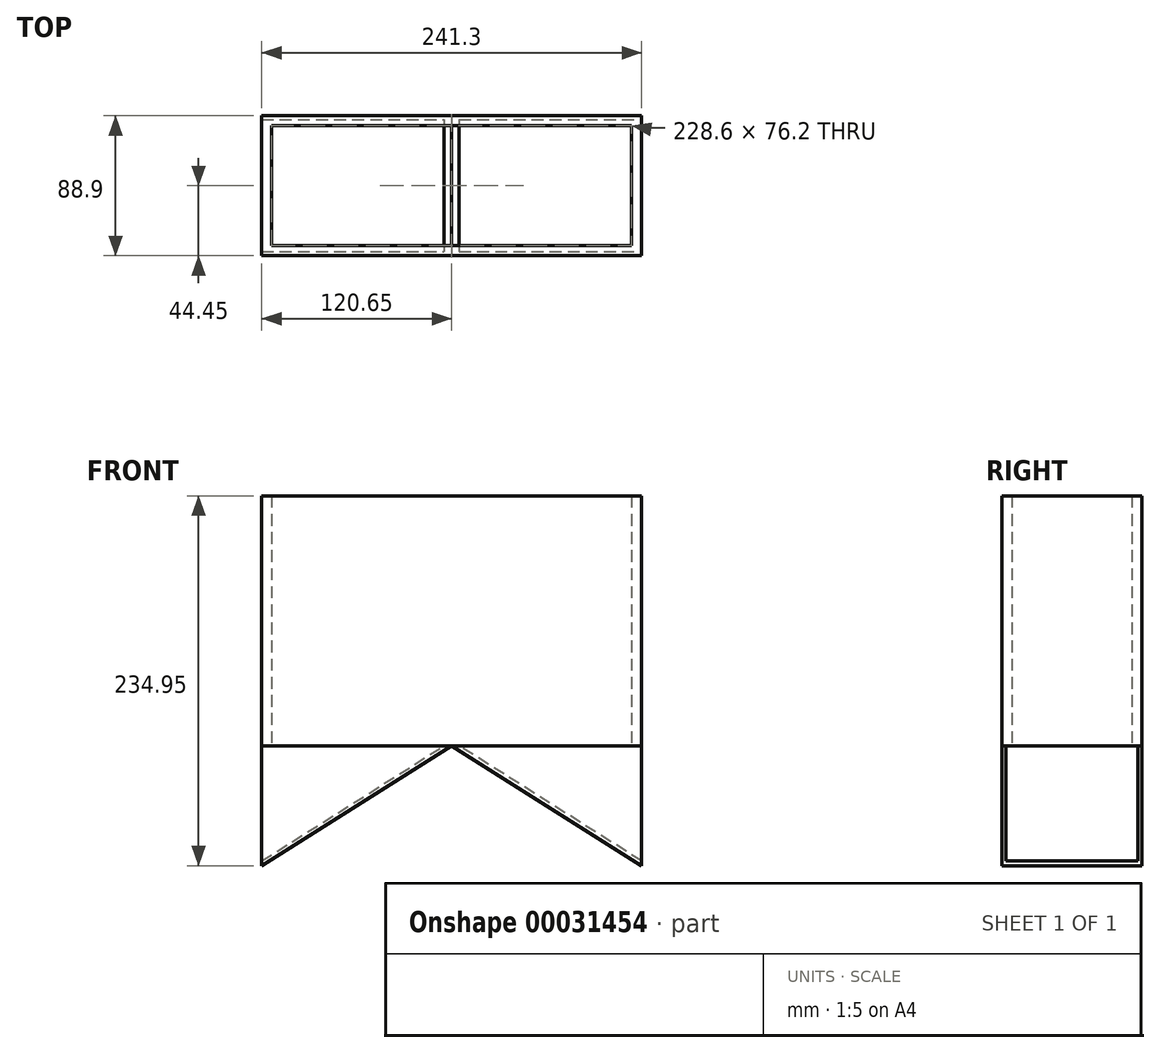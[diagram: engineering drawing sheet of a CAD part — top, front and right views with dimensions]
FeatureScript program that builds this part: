
annotation { "Feature Type Name" : "Feature", "Feature Type Description" : "" }
export const myFeature = defineFeature(function(context is Context, id is Id, definition is map)
    precondition{}
    {
        {
            var Q0;
            Q0=qCreatedBy(makeId("Top.planeOp"),FACE);
            var sketch = newSketch(context, id + "F0", { "sketchPlane" : qUnion([Q0])});
            skLineSegment(sketch, "E0.rect.bottom", {"start": v(-120.65, -44.45) * mm, "end": v(120.65, -44.45) * mm});
            skLineSegment(sketch, "E0.rect.top", {"start": v(-120.65, 44.45) * mm, "end": v(120.65, 44.45) * mm});
            skLineSegment(sketch, "E0.rect.left", {"start": v(-120.65, -44.45) * mm, "end": v(-120.65, 44.45) * mm});
            skLineSegment(sketch, "E0.rect.right", {"start": v(120.65, -44.45) * mm, "end": v(120.65, 44.45) * mm});
            skPoint(sketch, "E0.rect.middle", {"position": v(0, 0) * mm});
            skSolve(sketch);
        }
        {
            var Q0;
            Q0=makeQuery(id+"F0.imprint","IMPRINT",FACE,{"disambiguationData":[TD([[makeQuery(id+"F0.imprint","IMPRINT",EDGE,{"derivedFrom":sQuery(id+"F0.wireOp",EDGE,"E0.rect.bottom")}),1.0]])]});
            extrude(context, id + "F1", {"entities" : qUnion([Q0]), "depth" : 158.75 * mm});
        }
        {
            var Q0;
            Q0=makeQuery(id+"F1.opExtrude","CAP_FACE",FACE,{"disambiguationData":[OSD([sQuery(id+"F0.wireOp",EDGE,"E0.rect.bottom"),sQuery(id+"F0.wireOp",EDGE,"E0.rect.top"),sQuery(id+"F0.wireOp",EDGE,"E0.rect.left"),sQuery(id+"F0.wireOp",EDGE,"E0.rect.right")])],"isStart":false});
            shell(context, id + "F2", {"entities" : qUnion([Q0]), "thickness" : 6.35 * mm});
        }
        {
            var Q0;
            Q0=makeQuery(id+"F2.opShell","OFFSET_FACE",FACE,{"disambiguationData":[OSD([sQuery(id+"F0.wireOp",EDGE,"E0.rect.bottom"),sQuery(id+"F0.wireOp",EDGE,"E0.rect.top"),sQuery(id+"F0.wireOp",EDGE,"E0.rect.left"),sQuery(id+"F0.wireOp",EDGE,"E0.rect.right")])]});
            extrude(context, id + "F3", {"entities" : qUnion([Q0]), "operationType" : NewBodyOperationType.REMOVE, "oppositeDirection" : true, "depth" : 25.4 * mm});
        }
        {
            var Q0;
            Q0=makeQuery(id+"F1.opExtrude","SWEPT_FACE",FACE,{"disambiguationData":[OSD([sQuery(id+"F0.wireOp",EDGE,"E0.rect.bottom")])]});
            var sketch = newSketch(context, id + "F4", { "sketchPlane" : qUnion([Q0])});
            skLineSegment(sketch, "E1", {"start": v(-120.65, 0) * mm, "end": v(-120.65, -76.2) * mm});
            skLineSegment(sketch, "E2", {"start": v(-120.65, -76.2) * mm, "end": v(0, 0) * mm});
            skLineSegment(sketch, "E3", {"start": v(0, 0) * mm, "end": v(-120.65, 0) * mm});
            skLineSegment(sketch, "E4.MirrorCS", {"start": v(0, 0) * mm, "end": v(120.65, 0) * mm});
            skLineSegment(sketch, "E5.MirrorCS", {"start": v(120.65, 0) * mm, "end": v(120.65, -76.2) * mm});
            skLineSegment(sketch, "E6.MirrorCS", {"start": v(120.65, -76.2) * mm, "end": v(0, 0) * mm});
            skSolve(sketch);
        }
        {
            var Q0;
            Q0=makeQuery(id+"F4.imprint","IMPRINT",FACE,{"disambiguationData":[TD([[makeQuery(id+"F4.imprint","IMPRINT",EDGE,{"derivedFrom":sQuery(id+"F4.wireOp",EDGE,"E1")}),1.0]])]});
            var Q1;
            Q1=makeQuery(id+"F4.imprint","IMPRINT",FACE,{"disambiguationData":[TD([[makeQuery(id+"F4.imprint","IMPRINT",EDGE,{"derivedFrom":sQuery(id+"F4.wireOp",EDGE,"E4.MirrorCS")}),-1.0]])]});
            extrude(context, id + "F5", {"entities" : qUnion([Q0, Q1]), "oppositeDirection" : true, "depth" : 88.9 * mm});
        }
        {
            var Q0;
            Q0=makeQuery(id+"F5.opExtrude","SWEPT_FACE",FACE,{"disambiguationData":[OSD([sQuery(id+"F4.wireOp",EDGE,"E1")])]});
            var Q1;
            Q1=makeQuery(id+"F5.opExtrude","SWEPT_FACE",FACE,{"disambiguationData":[OSD([sQuery(id+"F4.wireOp",EDGE,"E3")])]});
            var Q2;
            Q2=makeQuery(id+"F5.opExtrude","SWEPT_FACE",FACE,{"disambiguationData":[OSD([sQuery(id+"F4.wireOp",EDGE,"E4.MirrorCS")])]});
            var Q3;
            Q3=makeQuery(id+"F5.opExtrude","SWEPT_FACE",FACE,{"disambiguationData":[OSD([sQuery(id+"F4.wireOp",EDGE,"E5.MirrorCS")])]});
            shell(context, id + "F6", {"entities" : qUnion([Q0, Q1, Q2, Q3]), "thickness" : 2.54 * mm});
        }
    });
